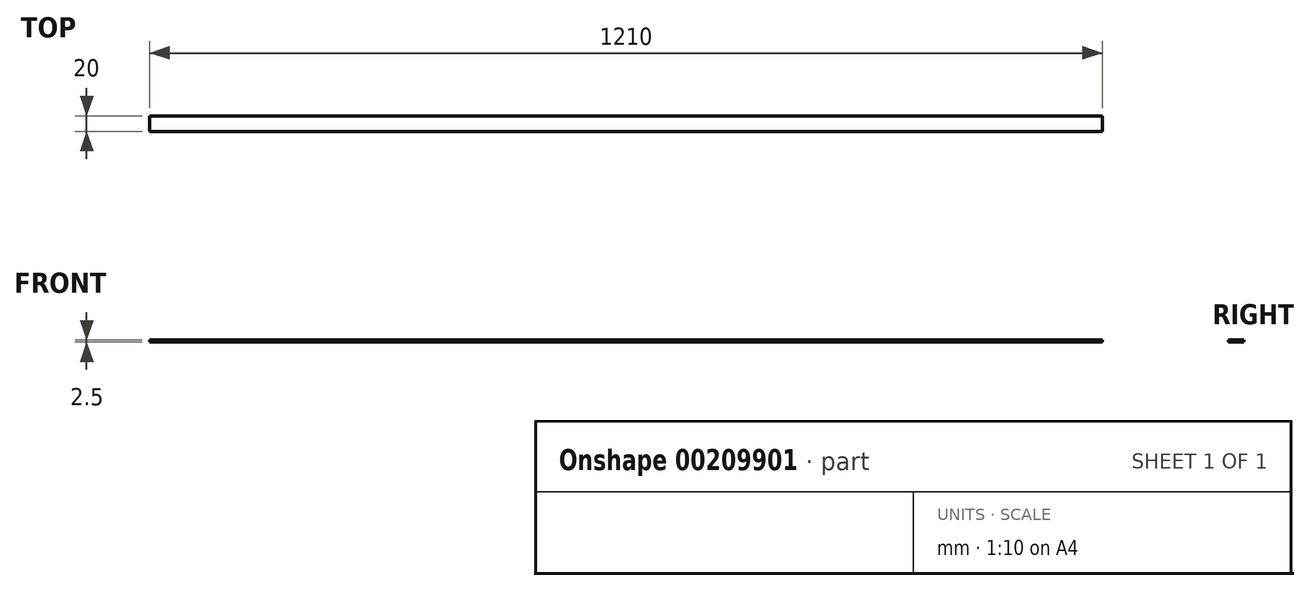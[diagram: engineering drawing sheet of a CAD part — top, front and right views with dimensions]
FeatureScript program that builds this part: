
annotation { "Feature Type Name" : "Feature", "Feature Type Description" : "" }
export const myFeature = defineFeature(function(context is Context, id is Id, definition is map)
    precondition{}
    {
        {
            var Q0;
            Q0=qCreatedBy(makeId("Top.planeOp"),FACE);
            var sketch = newSketch(context, id + "F0", { "sketchPlane" : qUnion([Q0])});
            skLineSegment(sketch, "E0.bottom", {"start": v(-605, 10) * mm, "end": v(605, 10) * mm});
            skLineSegment(sketch, "E0.top", {"start": v(-605, -10) * mm, "end": v(605, -10) * mm});
            skLineSegment(sketch, "E0.left", {"start": v(-605, 10) * mm, "end": v(-605, -10) * mm});
            skLineSegment(sketch, "E0.right", {"start": v(605, 10) * mm, "end": v(605, -10) * mm});
            skPoint(sketch, "E0.middle", {"position": v(0, 0) * mm});
            skSolve(sketch);
        }
        {
            var Q0;
            Q0=makeQuery(id+"F0.imprint","IMPRINT",FACE,{"disambiguationData":[TD([[makeQuery(id+"F0.imprint","IMPRINT",EDGE,{"derivedFrom":sQuery(id+"F0.wireOp",EDGE,"E0.bottom")}),-1.0]])]});
            extrude(context, id + "F1", {"entities" : qUnion([Q0]), "depth" : 2.5 * mm});
        }
    });
